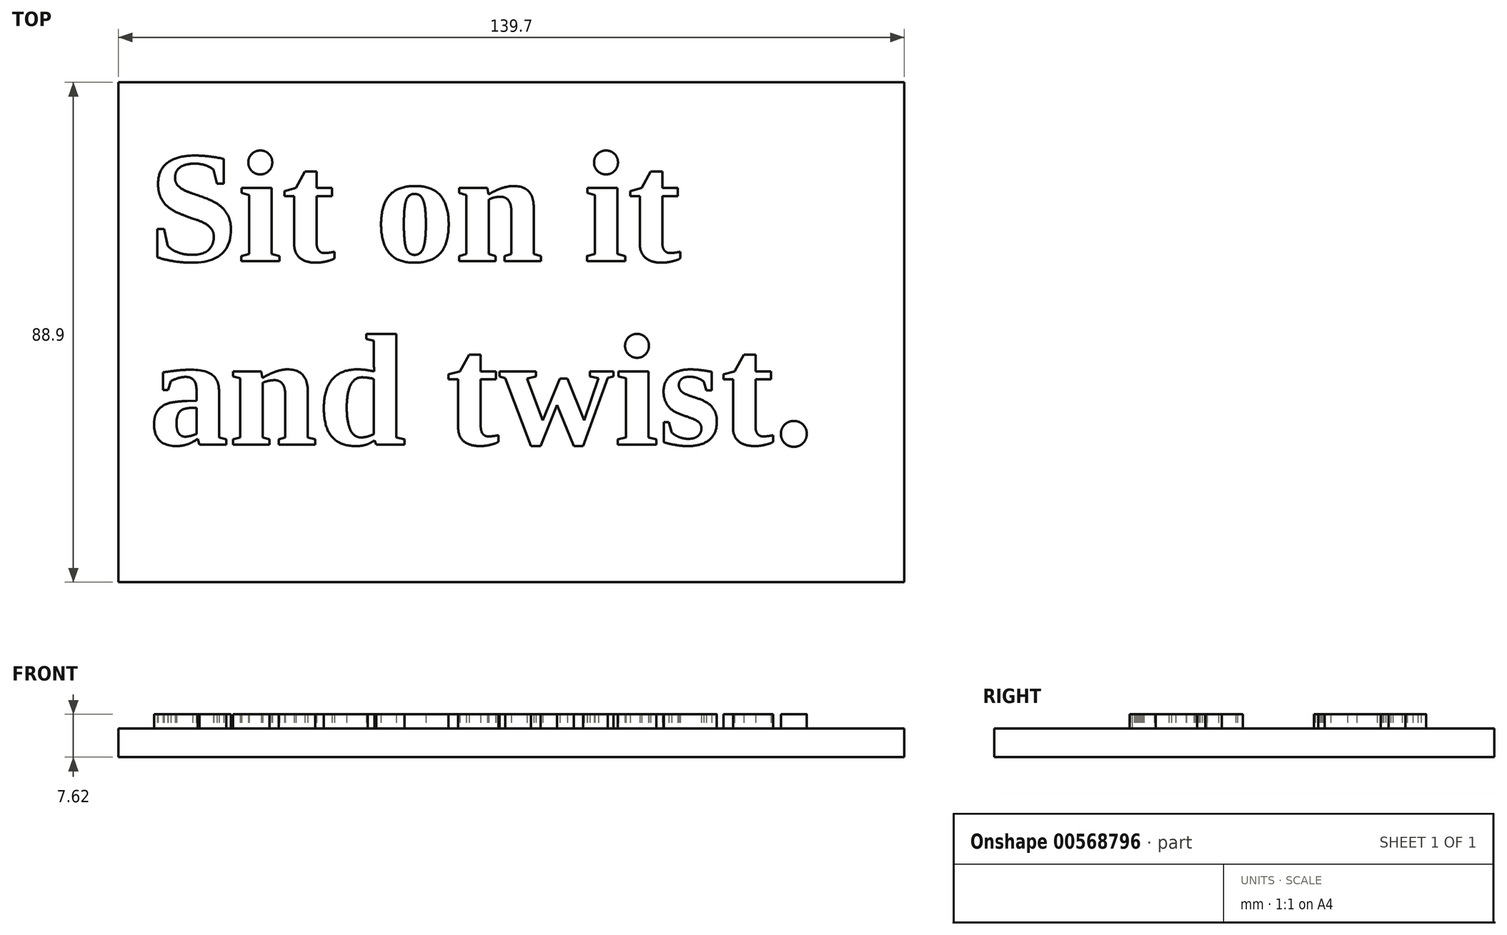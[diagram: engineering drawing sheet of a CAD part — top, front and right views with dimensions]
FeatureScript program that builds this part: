
annotation { "Feature Type Name" : "Feature", "Feature Type Description" : "" }
export const myFeature = defineFeature(function(context is Context, id is Id, definition is map)
    precondition{}
    {
        {
            var Q0;
            Q0=qCreatedBy(makeId("Top.planeOp"),FACE);
            var sketch = newSketch(context, id + "F0", { "sketchPlane" : qUnion([Q0])});
            skLineSegment(sketch, "E0.bottom", {"start": v(-69.85, -44.45) * mm, "end": v(69.85, -44.45) * mm});
            skLineSegment(sketch, "E0.top", {"start": v(-69.85, 44.45) * mm, "end": v(69.85, 44.45) * mm});
            skLineSegment(sketch, "E0.left", {"start": v(-69.85, -44.45) * mm, "end": v(-69.85, 44.45) * mm});
            skLineSegment(sketch, "E0.right", {"start": v(69.85, -44.45) * mm, "end": v(69.85, 44.45) * mm});
            skPoint(sketch, "E0.middle", {"position": v(0, 0) * mm});
            skSolve(sketch);
        }
        {
            var Q0;
            Q0=makeQuery(id+"F0.imprint","IMPRINT",FACE,{"disambiguationData":[TD([[makeQuery(id+"F0.imprint","IMPRINT",EDGE,{"derivedFrom":sQuery(id+"F0.wireOp",EDGE,"E0.bottom")}),1.0]])]});
            var sketch = newSketch(context, id + "F1", { "sketchPlane" : qUnion([Q0])});
            skText(sketch, "E1", { "text": "Sit on it \nand twist.", "fontName": "Tinos-Bold.ttf"});
            const initialGuessF1  = {"E1": [-0.06442, 0.01265, 1, 0, 0.02042]};
            skSetInitialGuess(sketch, initialGuessF1);
            skSolve(sketch);
        }
        {
            var Q0;
            Q0 = qSketchRegion(id + "F0", true);
            extrude(context, id + "F2", {"entities" : qUnion([Q0]), "depth" : 5.08 * mm, "offsetDistance" : 25.4 * mm});
        }
        {
            var Q0;
            Q0 = qSketchRegion(id + "F1", true);
            extrude(context, id + "F3", {"entities" : qUnion([Q0]), "operationType" : NewBodyOperationType.ADD, "depth" : 7.62 * mm, "offsetDistance" : 25.4 * mm});
        }
    });
